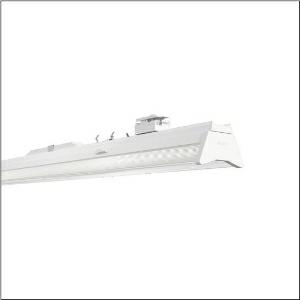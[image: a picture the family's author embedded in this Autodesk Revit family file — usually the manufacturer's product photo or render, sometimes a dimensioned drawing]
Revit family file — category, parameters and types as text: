
# Revit family: licross_11_performance_mo_51td16cn69xg
name_source: partatom
category: Lighting Fixtures
units: mm (PartAtom-declared; Revit-internal decimal feet)

## family parameters
Cut with Voids When Loaded = No
Host = Face
Light Source = No
Part Type = Normal
Room Calculation Point = No
Round Connector Dimension = Use Diameter
Shared = No

## types (1)
- --- (1 x LED, 8960 lm, 49.4 W, 6500K)
    Apparent Load = 49 VA
    CIE Flux Codes = 66 88 96 79 100
    Color Rendering = 80
    Color Temperature = 6500K
    Default Elevation = 1800 mm
    Description = Licross 11 Performance MO, luminaire insert, of sheet steel, galvanised, coil coated, white, length: 1.500mm, width: 120mm, height: 123mm, LED rated luminous flux: 8.960lm, light colour: 865, SDCM (Standard Deviation of Colour Matching)MacAdam ≤ 2 SDCM (initial), control gear: ON/OFF Multilumen, CLOi, with plug, 3-pole, with phase selection, mains connection: 220..240V, AC, 50/60Hz, start of lifetime: 49W, end of service life: 55W, internal wiring halogen-free, primary light control with lens, of plastic, primary optical cover: cover, of PMMA, light emission: direct/indirect distribution, primary light characteristic: symmetric, protection rating (complete): IP54, insulation class (complete): insulation class I (protective earthing), certification: CE, ENEC, VDE, UKCA, protection symbol: D if used in an environment with non-conductive dust loads with corresponding accessories, impact resistance: IK06, permissible ambient temperature for indoor applications: -35..+40°C, corresponds to IFS (International Featured Standards) requirements for safety and quality in the food industry, reducing of maximum allowable ambient temperature of 5°C with ceiling mounting, LABS conformity tested according to VDMA 24364:2018-05, The light source and the operating device comply with the requirements of the Ecodesign Regulation (EU) 2019/2020 and are replaceable in accordance with this regulation, packaging unit: 1 piece
    Height = 114 mm
    Lamp = 1 x LED
    Lamp Light Flux = 8960 lm
    Lamp Power = 49.4 W
    Lamp count = 1
    Length = 1500 mm
    Luminous efficacy = 181 lm/W
    Manufacturer = Siteco
    ModVariant = No
    Model = 51TD16CN69XG
    Mounting Place = Ceiling
    Mounting Type = Pendant
    Number of Poles = 1
    OnlyDefault = Yes
    Power Factor = 1
    Product Name = Licross 11 Performance MO
    Product group = luminaire insert | ceiling pendant
    ProductGroupID = 901
    Protection Class = Protection class I
    Protection Degree = IP 54
    RLX_Detail_Level = 1
    RLX_Emergency_Light_Flux = 0 lm
    RLX_Emergency_Type = 0
    RLX_Emergency_Type_DB = No
    RlxData = <blob elided: 32129 chars, md5=ca29168a>
    Socket = socket
    Standby Power = 0 W
    System Light Flux = 8960 lm
    System Power = 49 W
    Type Comments = factory setting: luminous flux: 100 % | (A | C | E) | 113 mA
    Type Image = l_1256138.jpg
    URL = http://relux.com
    VarID = @adj_038197
    Voltage = 0 V
    Weight = 0.00 kg
    Width = 120 mm

## geometry (parser evidence)
native form markers: Blend x4, Sweep x11
no freeform markers — native parametric forms only
